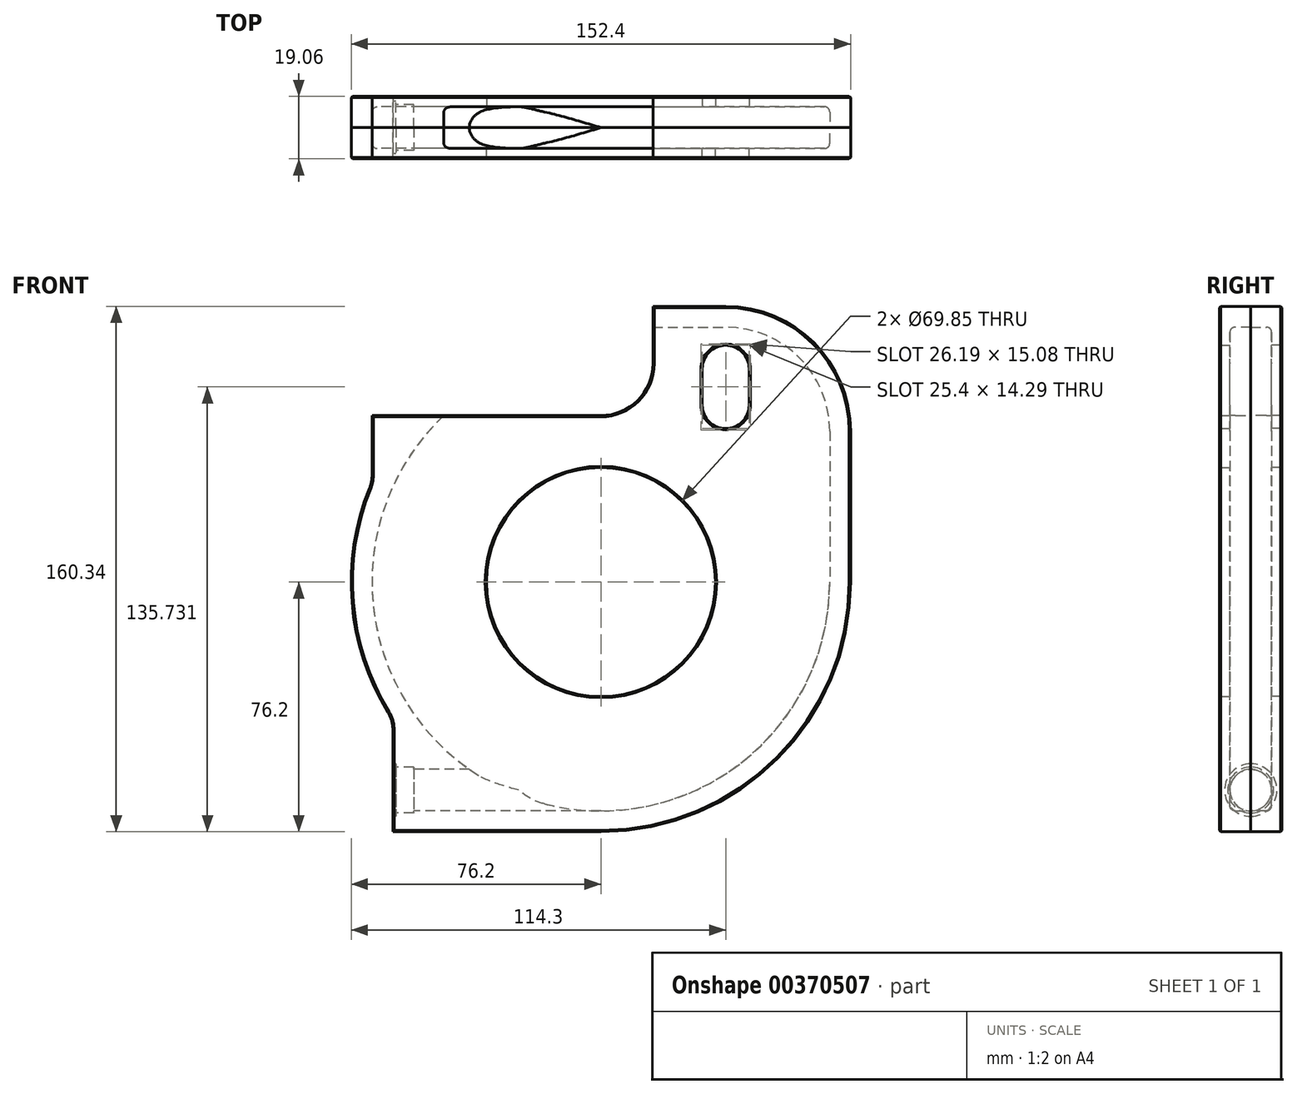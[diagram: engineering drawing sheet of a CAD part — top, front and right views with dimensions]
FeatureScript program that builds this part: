
annotation { "Feature Type Name" : "Feature", "Feature Type Description" : "" }
export const myFeature = defineFeature(function(context is Context, id is Id, definition is map)
    precondition{}
    {
        {
            var Q0;
            Q0=qCreatedBy(makeId("Front.planeOp"),FACE);
            var sketch = newSketch(context, id + "F0", { "sketchPlane" : qUnion([Q0])});
            skCircle(sketch, "E0", {"center": v(0, 0) * mm, "radius": 34.93 * mm});
            skArc(sketch, "E1", {"start": v(0, -76.2) * mm, "mid": v(53.88, -53.88) * mm, "end": v(76.2, 0) * mm});
            skLineSegment(sketch, "E2", {"start": v(76.2, 0) * mm, "end": v(76.2, 46.04) * mm});
            skLineSegment(sketch, "E3", {"start": v(-69.85, 50.8) * mm, "end": v(0, 50.8) * mm});
            skLineSegment(sketch, "E4", {"start": v(0, -76.2) * mm, "end": v(-63.5, -76.2) * mm});
            skLineSegment(sketch, "E5", {"start": v(-63.5, -76.2) * mm, "end": v(-63.5, -44.9) * mm});
            skLineSegment(sketch, "E6", {"start": v(38.1, 84.14) * mm, "end": v(15.87, 84.14) * mm});
            skLineSegment(sketch, "E7", {"start": v(15.87, 84.14) * mm, "end": v(15.87, 66.67) * mm});
            skArc(sketch, "E8", {"start": v(0, 50.8) * mm, "mid": v(11.23, 55.45) * mm, "end": v(15.87, 66.67) * mm});
            skPoint(sketch, "E9.visualSharp", {"position": v(76.2, 84.14) * mm});
            skArc(sketch, "E9.filletArc", {"start": v(76.2, 46.04) * mm, "mid": v(65.04, 72.98) * mm, "end": v(38.1, 84.14) * mm});
            skArc(sketch, "E10.trimOffspring", {"start": v(-70.56, 28.78) * mm, "mid": v(-75.94, -6.24) * mm, "end": v(-64.91, -39.91) * mm});
            skLineSegment(sketch, "E11", {"start": v(-69.85, 50.8) * mm, "end": v(-69.85, 32.38) * mm});
            skPoint(sketch, "E12.visualSharp", {"position": v(-69.85, 30.45) * mm});
            skArc(sketch, "E12.filletArc", {"start": v(-70.56, 28.78) * mm, "mid": v(-70.03, 30.55) * mm, "end": v(-69.85, 32.38) * mm});
            skPoint(sketch, "E13.visualSharp", {"position": v(-63.5, -42.12) * mm});
            skArc(sketch, "E13.filletArc", {"start": v(-63.5, -44.9) * mm, "mid": v(-63.86, -42.3) * mm, "end": v(-64.91, -39.91) * mm});
            skLineSegment(sketch, "E14", {"start": v(0, 0) * mm, "end": v(38.1, 0) * mm, "construction": true});
            skLineSegment(sketch, "E15", {"start": v(30.96, 53.98) * mm, "end": v(30.96, 65.09) * mm});
            skLineSegment(sketch, "E16", {"start": v(45.24, 53.98) * mm, "end": v(45.24, 65.09) * mm});
            skArc(sketch, "E17", {"start": v(30.96, 65.09) * mm, "mid": v(38.1, 72.23) * mm, "end": v(45.24, 65.09) * mm});
            skArc(sketch, "E18", {"start": v(45.24, 53.98) * mm, "mid": v(38.1, 46.83) * mm, "end": v(30.96, 53.98) * mm});
            skSolve(sketch);
        }
        {
            var Q0;
            Q0=qCreatedBy(makeId("Front.planeOp"),FACE);
            var sketch = newSketch(context, id + "F1", { "sketchPlane" : qUnion([Q0])});
            skArc(sketch, "E19", {"start": v(0, 69.85) * mm, "mid": v(-49.4, -49.4) * mm, "end": v(69.85, 0) * mm});
            skLineSegment(sketch, "E20", {"start": v(0, 69.85) * mm, "end": v(0, 77.79) * mm});
            skLineSegment(sketch, "E21", {"start": v(0, 77.79) * mm, "end": v(38.1, 77.79) * mm});
            skLineSegment(sketch, "E22", {"start": v(69.85, 46.04) * mm, "end": v(69.85, 0) * mm});
            skPoint(sketch, "E23.visualSharp", {"position": v(69.85, 77.79) * mm});
            skArc(sketch, "E23.filletArc", {"start": v(69.85, 46.04) * mm, "mid": v(60.55, 68.49) * mm, "end": v(38.1, 77.79) * mm});
            skSolve(sketch);
        }
        {
            var Q0;
            Q0=makeQuery(id+"F1.imprint","IMPRINT",FACE,{"disambiguationData":[TD([[makeQuery(id+"F1.imprint","IMPRINT",EDGE,{"derivedFrom":sQuery(id+"F1.wireOp",EDGE,"E19")}),1.0]])]});
            extrude(context, id + "F2", {"entities" : qUnion([Q0]), "depth" : 6.35 * mm});
        }
        {
            var Q0;
            Q0=makeQuery(id+"F2.opExtrude","CAP_EDGE",EDGE,{"disambiguationData":[OSD([sQuery(id+"F1.wireOp",EDGE,"E23.filletArc")])],"isStart":false});
            fillet(context, id + "F3", {"entities" : qUnion([Q0]), "radius" : 1.59 * mm, "tangentPropagation" : true, "allowEdgeOverflow" : false});
        }
        {
            var Q0;
            Q0=makeQuery(id+"F0.imprint","IMPRINT",FACE,{"disambiguationData":[TD([[makeQuery(id+"F0.imprint","IMPRINT",EDGE,{"derivedFrom":sQuery(id+"F0.wireOp",EDGE,"E0")}),-1.0]])]});
            extrude(context, id + "F4", {"entities" : qUnion([Q0]), "depth" : 9.52 * mm});
        }
        {
            var Q0;
            Q0=makeQuery(id+"F2.opExtrude","SWEPT_BODY",BODY,{"disambiguationData":[OSD([sQuery(id+"F1.wireOp",EDGE,"E19"),sQuery(id+"F1.wireOp",EDGE,"E20"),sQuery(id+"F1.wireOp",EDGE,"E21"),sQuery(id+"F1.wireOp",EDGE,"E22"),sQuery(id+"F1.wireOp",EDGE,"E23.filletArc")])]});
            var Q1;
            Q1=makeQuery(id+"F4.opExtrude","SWEPT_BODY",BODY,{"disambiguationData":[OSD([sQuery(id+"F0.wireOp",EDGE,"E0"),sQuery(id+"F0.wireOp",EDGE,"E1"),sQuery(id+"F0.wireOp",EDGE,"E2"),sQuery(id+"F0.wireOp",EDGE,"E3"),sQuery(id+"F0.wireOp",EDGE,"E4"),sQuery(id+"F0.wireOp",EDGE,"E5"),sQuery(id+"F0.wireOp",EDGE,"E6"),sQuery(id+"F0.wireOp",EDGE,"E7"),sQuery(id+"F0.wireOp",EDGE,"E8"),sQuery(id+"F0.wireOp",EDGE,"E9.filletArc"),sQuery(id+"F0.wireOp",EDGE,"E10.trimOffspring"),sQuery(id+"F0.wireOp",EDGE,"E11"),sQuery(id+"F0.wireOp",EDGE,"E12.filletArc"),sQuery(id+"F0.wireOp",EDGE,"E13.filletArc")])]});
            booleanBodies(context, id + "F5", {"operationType" : BooleanOperationType.SUBTRACTION, "tools" : qUnion([Q0]), "targets" : qUnion([Q1])});
        }
        {
            var Q0;
            Q0=makeQuery(id+"F4.opExtrude","SWEPT_BODY",BODY,{"disambiguationData":[OSD([sQuery(id+"F0.wireOp",EDGE,"E0"),sQuery(id+"F0.wireOp",EDGE,"E1"),sQuery(id+"F0.wireOp",EDGE,"E2"),sQuery(id+"F0.wireOp",EDGE,"E3"),sQuery(id+"F0.wireOp",EDGE,"E4"),sQuery(id+"F0.wireOp",EDGE,"E5"),sQuery(id+"F0.wireOp",EDGE,"E6"),sQuery(id+"F0.wireOp",EDGE,"E7"),sQuery(id+"F0.wireOp",EDGE,"E8"),sQuery(id+"F0.wireOp",EDGE,"E9.filletArc"),sQuery(id+"F0.wireOp",EDGE,"E10.trimOffspring"),sQuery(id+"F0.wireOp",EDGE,"E11"),sQuery(id+"F0.wireOp",EDGE,"E12.filletArc"),sQuery(id+"F0.wireOp",EDGE,"E13.filletArc")])]});
            var Q1;
            Q1=makeQuery(id+"F4.opExtrude","CAP_FACE",FACE,{"disambiguationData":[OSD([sQuery(id+"F0.wireOp",EDGE,"E0"),sQuery(id+"F0.wireOp",EDGE,"E1"),sQuery(id+"F0.wireOp",EDGE,"E2"),sQuery(id+"F0.wireOp",EDGE,"E3"),sQuery(id+"F0.wireOp",EDGE,"E4"),sQuery(id+"F0.wireOp",EDGE,"E5"),sQuery(id+"F0.wireOp",EDGE,"E6"),sQuery(id+"F0.wireOp",EDGE,"E7"),sQuery(id+"F0.wireOp",EDGE,"E8"),sQuery(id+"F0.wireOp",EDGE,"E9.filletArc"),sQuery(id+"F0.wireOp",EDGE,"E10.trimOffspring"),sQuery(id+"F0.wireOp",EDGE,"E11"),sQuery(id+"F0.wireOp",EDGE,"E12.filletArc"),sQuery(id+"F0.wireOp",EDGE,"E13.filletArc")])],"isStart":true});
            mirror(context, id + "F6", {"entities" : qUnion([Q0]), "mirrorPlane" : qUnion([Q1])});
        }
        {
            var Q0;
            Q0=makeQuery(id+"F4.opExtrude","CAP_FACE",FACE,{"disambiguationData":[OSD([sQuery(id+"F0.wireOp",EDGE,"E0"),sQuery(id+"F0.wireOp",EDGE,"E1"),sQuery(id+"F0.wireOp",EDGE,"E2"),sQuery(id+"F0.wireOp",EDGE,"E3"),sQuery(id+"F0.wireOp",EDGE,"E4"),sQuery(id+"F0.wireOp",EDGE,"E5"),sQuery(id+"F0.wireOp",EDGE,"E6"),sQuery(id+"F0.wireOp",EDGE,"E7"),sQuery(id+"F0.wireOp",EDGE,"E8"),sQuery(id+"F0.wireOp",EDGE,"E9.filletArc"),sQuery(id+"F0.wireOp",EDGE,"E10.trimOffspring"),sQuery(id+"F0.wireOp",EDGE,"E11"),sQuery(id+"F0.wireOp",EDGE,"E12.filletArc"),sQuery(id+"F0.wireOp",EDGE,"E13.filletArc"),sQuery(id+"F0.wireOp",EDGE,"E15"),sQuery(id+"F0.wireOp",EDGE,"E16"),sQuery(id+"F0.wireOp",EDGE,"E17"),sQuery(id+"F0.wireOp",EDGE,"E18")])],"isStart":false});
            var Q1;
            Q1=makeQuery(id+"F6.opPattern","COPY",FACE,{"derivedFrom":makeQuery(id+"F4.opExtrude","CAP_FACE",FACE,{"disambiguationData":[OSD([sQuery(id+"F0.wireOp",EDGE,"E0"),sQuery(id+"F0.wireOp",EDGE,"E1"),sQuery(id+"F0.wireOp",EDGE,"E2"),sQuery(id+"F0.wireOp",EDGE,"E3"),sQuery(id+"F0.wireOp",EDGE,"E4"),sQuery(id+"F0.wireOp",EDGE,"E5"),sQuery(id+"F0.wireOp",EDGE,"E6"),sQuery(id+"F0.wireOp",EDGE,"E7"),sQuery(id+"F0.wireOp",EDGE,"E8"),sQuery(id+"F0.wireOp",EDGE,"E9.filletArc"),sQuery(id+"F0.wireOp",EDGE,"E10.trimOffspring"),sQuery(id+"F0.wireOp",EDGE,"E11"),sQuery(id+"F0.wireOp",EDGE,"E12.filletArc"),sQuery(id+"F0.wireOp",EDGE,"E13.filletArc"),sQuery(id+"F0.wireOp",EDGE,"E15"),sQuery(id+"F0.wireOp",EDGE,"E16"),sQuery(id+"F0.wireOp",EDGE,"E17"),sQuery(id+"F0.wireOp",EDGE,"E18")])],"isStart":false}),"instanceName":"1"});
            chamfer(context, id + "F7", {"entities" : qUnion([Q0, Q1]), "width" : 0.4 * mm, "tangentPropagation" : true});
        }
        {
            var Q0;
            Q0=qCreatedBy(makeId("Front.planeOp"),FACE);
            var sketch = newSketch(context, id + "F8", { "sketchPlane" : qUnion([Q0])});
            skLineSegment(sketch, "E24", {"start": v(9.41, -63.5) * mm, "end": v(-86.1, -63.5) * mm, "construction": true});
            skLineSegment(sketch, "E25", {"start": v(0, -63.5) * mm, "end": v(0, -57.15) * mm});
            skLineSegment(sketch, "E26", {"start": v(0, -57.15) * mm, "end": v(-57.15, -57.15) * mm});
            skLineSegment(sketch, "E27", {"start": v(-57.15, -57.15) * mm, "end": v(-57.15, -56.5) * mm});
            skLineSegment(sketch, "E28", {"start": v(-57.15, -56.5) * mm, "end": v(-62.5, -56.5) * mm});
            skLineSegment(sketch, "E29", {"start": v(-62.5, -55.5) * mm, "end": v(-63.5, -55.5) * mm});
            skLineSegment(sketch, "E30", {"start": v(-63.5, -55.5) * mm, "end": v(-63.5, -63.5) * mm});
            skLineSegment(sketch, "E31", {"start": v(-62.5, -55.5) * mm, "end": v(-62.5, -56.5) * mm});
            skLineSegment(sketch, "E32", {"start": v(0, -63.5) * mm, "end": v(-63.5, -63.5) * mm});
            skSolve(sketch);
        }
        {
            var Q0;
            Q0=makeQuery(id+"F8.imprint","IMPRINT",FACE,{"disambiguationData":[TD([[makeQuery(id+"F8.imprint","IMPRINT",EDGE,{"derivedFrom":sQuery(id+"F8.wireOp",EDGE,"E25")}),1.0]])]});
            var Q1;
            Q1=sQuery(id+"F8.wireOp",EDGE,"E24");
            revolve(context, id + "F9", {"operationType" : NewBodyOperationType.REMOVE, "entities" : qUnion([Q0]), "axis" : qUnion([Q1]), "revolveType" : RevolveType.FULL, "oppositeDirection" : true});
        }
    });
